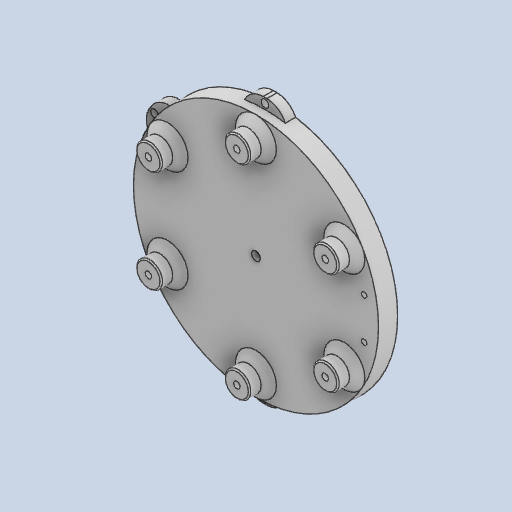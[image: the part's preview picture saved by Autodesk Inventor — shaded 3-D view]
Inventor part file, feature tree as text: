
AUTODESK INVENTOR PART (.ipt)
format: ipt  version: 2024 (Build 280153000, 153)  size: 727,552 bytes
history: native  units: mm
features: extrude x9, sketch x9, reference x7, other x7, pattern_circular x5, plane x3, fillet x3, projected_geometry x2, chamfer x1
ambient origin geometry x8: Origin, YZ Plane, XZ Plane, XY Plane, X Axis, Y Axis, Z Axis, Center Point
bodies: Solid1 (feature_tree)
feature tree (46):
  plane  "Work Plane1"
  extrude  "Extrusion1"  Depth=15.0mm
  plane  "Work Plane2"
  extrude  "Extrusion2"  Depth=20.0mm TaperAngle=360.0deg
  sketch  "Sketch3"  dims[d8=10.0mm d9=0.0mm d11=10.0mm d12=0.0mm d13=60.0mm d14=360.0deg]
  plane  "Work Plane3"
  extrude  "Extrusion3"  Depth=10.0mm TaperAngle=0.0deg
  pattern_circular  "Circular Pattern1"  Count=6 Angle=360.0deg
  extrude  "Extrusion4"  Depth=60.0mm TaperAngle=360.0deg
  pattern_circular  "Circular Pattern2"  [2 undecoded]
  extrude  "Extrusion5"  Depth=8.0mm TaperAngle=45.0deg
  fillet  "Fillet1"  Radius=7.0mm
  fillet  "Fillet3"  [1 undecoded]
  fillet  "Fillet4"  Radius=60.0mm
  chamfer  "Chamfer1"  Distance=5.1mm
  extrude  "Extrusion6"  Depth=10.0mm TaperAngle=0.0deg
  pattern_circular  "Circular Pattern3"  Count=6 Angle=360.0deg
  extrude  "Extrusion7"  Depth=8.0mm
  pattern_circular  "Circular Pattern4"  [2 undecoded]
  pattern_circular  "Circular Pattern5"  Count=6 Angle=360.0deg
  extrude  "Extrusion9"  TaperAngle=0.0deg  [1 undecoded]
  extrude  "Extrusion10"  TaperAngle=0.0deg  [1 undecoded]
  sketch  "Sketch1"  dims[d0=15.0mm d1=0.0mm d2=26.0mm]
  reference  "Reference1"
  sketch  "Sketch2"  dims[d3=20.0mm d4=60.0mm d6=360.0deg]
  reference  "Reference6"
  reference  "Reference7"
  reference  "Reference8"
  reference  "Reference9"
  sketch  "Sketch4"  dims[d16=40.0mm d17=0.0mm d18=60.0mm d19=360.0deg]
  sketch  "Sketch5"  dims[d28=8.0mm d29=0.0mm]
  sketch  "Sketch6"  dims[d30=16.0mm]
  sketch  "Sketch7"  dims[d32=1.0mm]
  sketch  "Sketch9"  dims[d33=1.0mm]
  projected_geometry  "Projected Loop4"
  projected_geometry  "Projected Loop5"
  sketch  "Sketch10"  dims[d34=7.0mm d35=7.0mm d36=6.0mm d37=2.0mm d38=45.0deg d39=7.0mm d40=0.0mm d41=0.0mm d42=60.0mm d43=360.0deg d45=5.1mm d46=10.0mm d47=0.0mm d48=60.0mm d49=360.0deg d53=8.0mm d54=6.0mm d55=60.0mm d56=360.0deg d58=0.0mm d59=0.0mm d60=0.0mm d61=0.0mm d20=0.5mm d21=0.872665mm]
  reference  "Reference12"
  reference  "Reference13"
  other  "<userpath>\Documents\Inventor\robot arm\base-new\base_assembly.iam"
  other  "base_assembly.iam"
  other  "base-top-plate:1"
  other  "base_bearing_Circle:3"
  other  "base_bearing_Circle:5"
  other  "base-bearing-cap:2"
  other  "base-stepper-holder:1"
note: 7 required parameter values undecoded (feature->parameter linkage not recoverable at this tier; creation-order binding heuristic only, values carry confidence <= 0.55)
